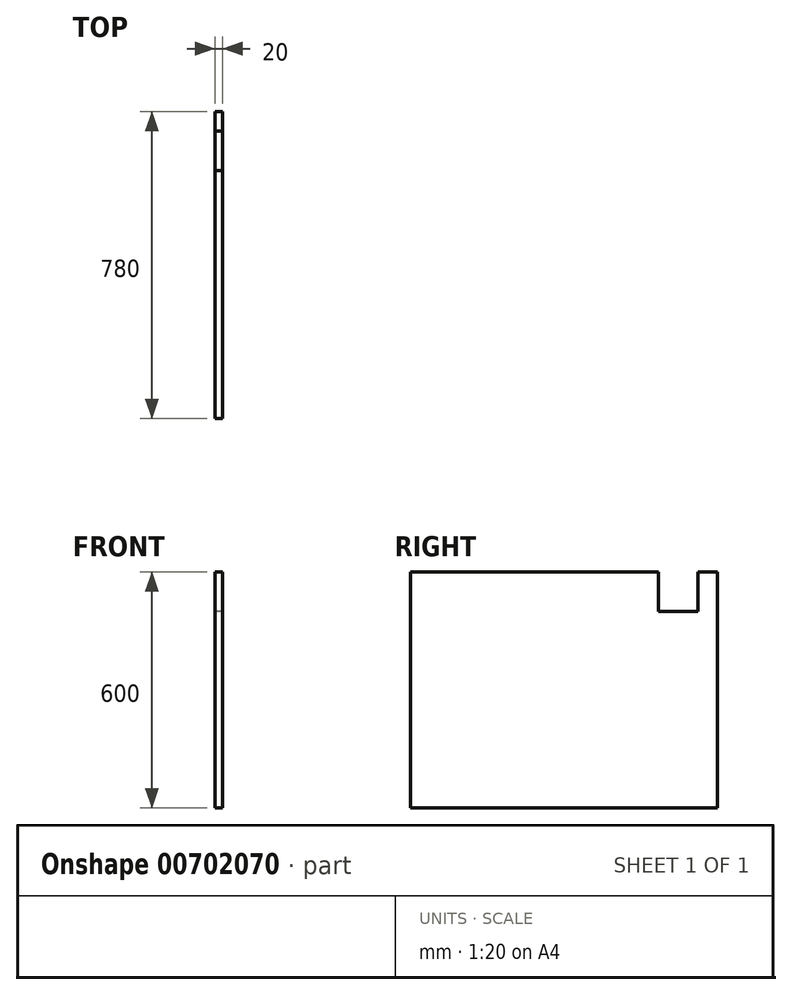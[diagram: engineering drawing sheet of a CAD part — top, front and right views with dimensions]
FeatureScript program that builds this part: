
annotation { "Feature Type Name" : "Feature", "Feature Type Description" : "" }
export const myFeature = defineFeature(function(context is Context, id is Id, definition is map)
    precondition{}
    {
        {
            var Q0;
            Q0=qCreatedBy(makeId("Right.planeOp"),FACE);
            var sketch = newSketch(context, id + "F0", { "sketchPlane" : qUnion([Q0])});
            skLineSegment(sketch, "E0.bottom", {"start": v(0, 0) * mm, "end": v(780, 0) * mm});
            skLineSegment(sketch, "E0.top", {"start": v(0, 600) * mm, "end": v(630, 600) * mm});
            skLineSegment(sketch, "E0.left", {"start": v(0, 0) * mm, "end": v(0, 600) * mm});
            skLineSegment(sketch, "E0.right", {"start": v(780, 0) * mm, "end": v(780, 600) * mm});
            skLineSegment(sketch, "E1", {"start": v(630, 600) * mm, "end": v(630, 500) * mm});
            skLineSegment(sketch, "E2", {"start": v(630, 500) * mm, "end": v(730, 500) * mm});
            skLineSegment(sketch, "E3", {"start": v(730, 500) * mm, "end": v(730, 600) * mm});
            skLineSegment(sketch, "E4.trimOffspring", {"start": v(730, 600) * mm, "end": v(780, 600) * mm});
            skSolve(sketch);
        }
        {
            var Q0;
            Q0 = qSketchRegion(id + "F0", true);
            extrude(context, id + "F1", {"entities" : qUnion([Q0]), "depth" : 20 * mm, "offsetDistance" : 25 * mm});
        }
    });
